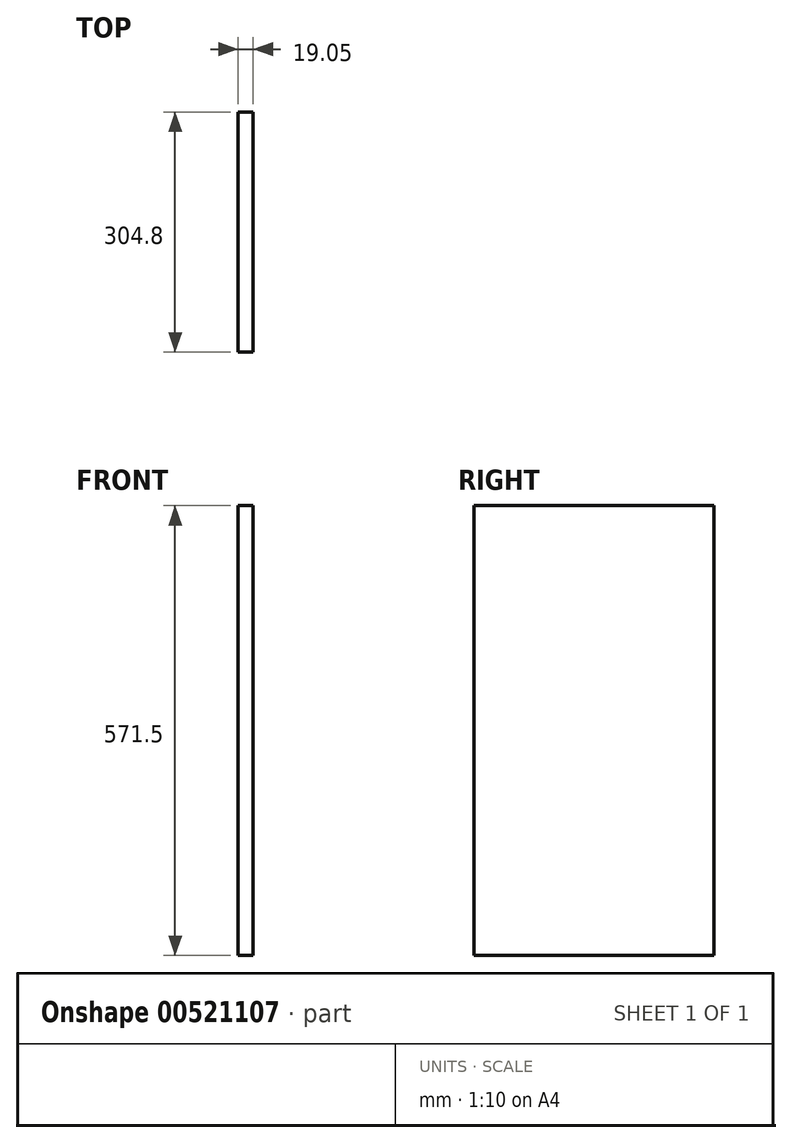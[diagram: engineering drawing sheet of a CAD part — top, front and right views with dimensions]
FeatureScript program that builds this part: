
annotation { "Feature Type Name" : "Feature", "Feature Type Description" : "" }
export const myFeature = defineFeature(function(context is Context, id is Id, definition is map)
    precondition{}
    {
        {
            var Q0;
            Q0=qCreatedBy(makeId("Right.planeOp"),FACE);
            var sketch = newSketch(context, id + "F0", { "sketchPlane" : qUnion([Q0])});
            skLineSegment(sketch, "E0.bottom", {"start": v(0, 0) * mm, "end": v(304.8, 0) * mm});
            skLineSegment(sketch, "E0.top", {"start": v(0, 571.5) * mm, "end": v(304.8, 571.5) * mm});
            skLineSegment(sketch, "E0.left", {"start": v(0, 0) * mm, "end": v(0, 571.5) * mm});
            skLineSegment(sketch, "E0.right", {"start": v(304.8, 0) * mm, "end": v(304.8, 571.5) * mm});
            skSolve(sketch);
        }
        {
            var Q0;
            Q0=makeQuery(id+"F0.imprint","IMPRINT",FACE,{"disambiguationData":[TD([[makeQuery(id+"F0.imprint","IMPRINT",EDGE,{"derivedFrom":sQuery(id+"F0.wireOp",EDGE,"E0.bottom")}),1.0]])]});
            extrude(context, id + "F1", {"entities" : qUnion([Q0]), "depth" : 19.05 * mm, "offsetDistance" : 25.4 * mm});
        }
    });
